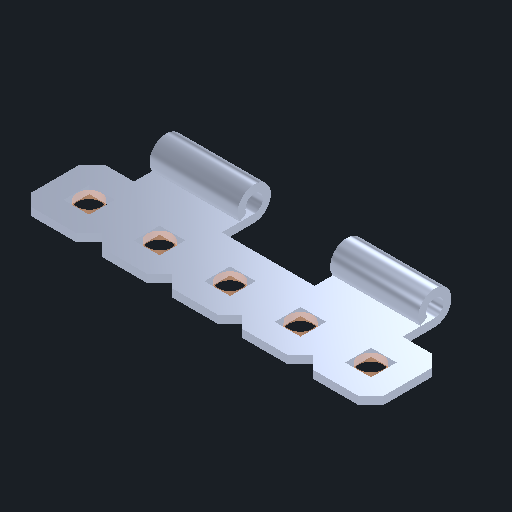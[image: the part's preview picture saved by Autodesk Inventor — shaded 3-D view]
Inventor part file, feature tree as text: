
AUTODESK INVENTOR PART (.ipt)
format: ipt  version: 2024 (Build 280153000, 153)  size: 212,480 bytes
history: native  units: in
note: dims shown in document units (in); Inventor stores cm internally (conversion verified against a paired STEP export)
features: other x7, extrude x5, pattern_linear x1, imported_body x1
ambient origin geometry x8: Origin, YZ Plane, XZ Plane, XY Plane, X Axis, Y Axis, Z Axis, Center Point
bodies: Body1 (feature_tree), Body2 (feature_tree), Body3 (feature_tree), Body4 (feature_tree), Body5 (feature_tree), Body6 (feature_tree)
feature tree (14):
  other  "Cut-Extrude3"
  other  "Bottom"
  pattern_linear  "Rectangular Pattern1"  Spacing1=0.046in  [1 undecoded]
  imported_body  "Base1"
  other  "Srf1"
  other  "Srf2"
  other  "Srf3"
  other  "Srf4"
  other  "Srf5"
  extrude  "ExtrusionSrf1"  Depth=0.5in
  extrude  "ExtrusionSrf2"  Depth=0.172in
  extrude  "ExtrusionSrf3"  [1 undecoded]
  extrude  "ExtrusionSrf4"  [1 undecoded]
  extrude  "ExtrusionSrf5"  [1 undecoded]
note: 4 required parameter values undecoded (feature->parameter linkage not recoverable at this tier; creation-order binding heuristic only, values carry confidence <= 0.55)
